# Revit family: TSL.R010
name_source: partatom
category: Specialty Equipment
revit_build: Autodesk Revit 2017 (Build: 20160225_1515(x64)
units: mm (PartAtom-declared; Revit-internal decimal feet)

## family parameters
Cut with Voids When Loaded = No
Host = Face
OmniClass Number = 23.40.20.21.34
OmniClass Title = Soap Holders, Dispensers
Part Type = Normal
Room Calculation Point = No
Round Connector Dimension = Use Diameter
Shared = No

## types (1)
- TSL.R010
    Assembly Code = C1030210
    AssetType = fixed
    BIMObjectName = TSL.R010
    Default Elevation = 0 mm  [stored 0 ft]
    DocumentationInstallationGuide = https://thesplashlab.com
    DocumentationLiterature = https://thesplashlab.com
    DocumentationMaintenance = https://thesplashlab.com
    DocumentationTechnical = https://thesplashlab.com
    DurationUnit = year
    ExpectedLife = 2
    Finish = Brushed
    Grade = 304
    IfcExportAs = IfcBuildingElementProxy
    IfcExportType = SOAPDISPENSER
    Keynote = N13/310
    Manufacturer = The Splash Lab
    ManufacturerURL = https://thesplashlab.com
    Material = Stainless Steel
    Model = TSL.R010
    ModelNumber = TSL.R010
    NBSReference = 45-35-72/358
    Name = TSL.R010
    NominalHeight = 113 mm
    NominalLength = 164 mm
    NominalWidth = 48 mm
    Product Documentation Link = https://thesplashlab.com
    Product O&M Link = https://thesplashlab.com
    Product Page Link = https://thesplashlab.com
    Product Specification Link = https://thesplashlab.com
    ProductInformation = https://thesplashlab.com
    Type Comments = Battery power, Satin finish
    TypeName = TSL.R010
    URL = https://thesplashlab.com
    Uniclass2 = 45-35-72/358
    Vent Connection = No
    Version = 0
    WarrantyDescription = 2 years from date of purchase
    WarrantyDurationParts = 1
    WarrantyDurationUnit = year
    WarrantyGuarantorParts = https://thesplashlab.com
    Waste Connection = No
    material = Steel-Lovair-Satin

note: [stored X ft] marks values corroborated as IEEE doubles in the binary element streams (Revit-internal decimal feet)

## geometry (parser evidence)
native form markers: Sweep x3
no freeform markers — native parametric forms only
